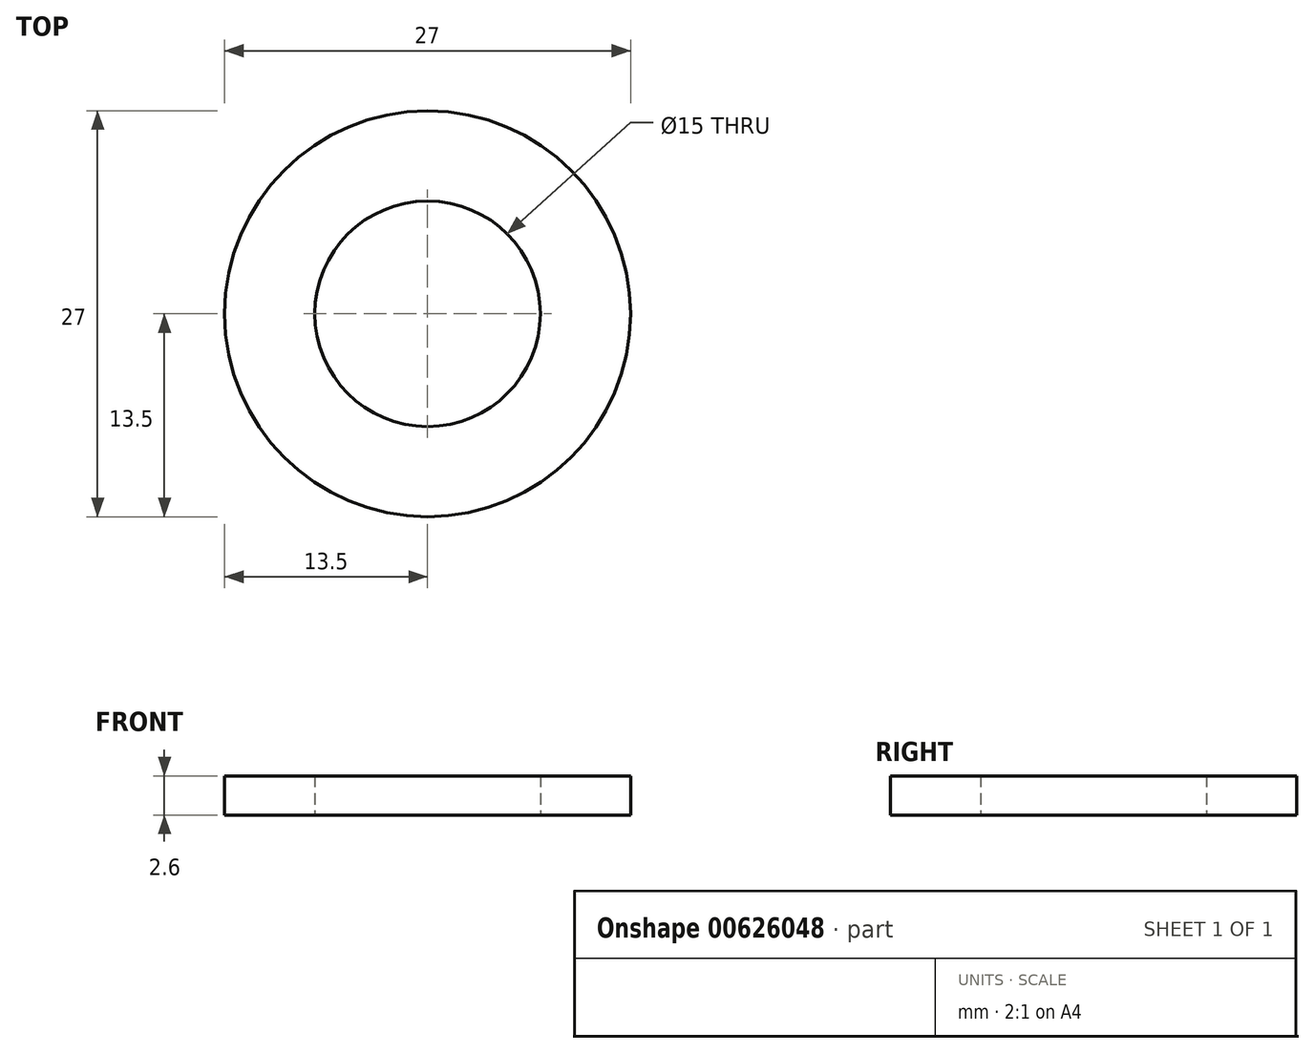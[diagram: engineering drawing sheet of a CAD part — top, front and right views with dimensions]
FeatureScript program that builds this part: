
annotation { "Feature Type Name" : "Feature", "Feature Type Description" : "" }
export const myFeature = defineFeature(function(context is Context, id is Id, definition is map)
    precondition{}
    {
        {
            var Q0;
            Q0=qCreatedBy(makeId("Top.planeOp"),FACE);
            var sketch = newSketch(context, id + "F0", { "sketchPlane" : qUnion([Q0])});
            skCircle(sketch, "E0", {"center": v(0, 0) * mm, "radius": 7.5 * mm});
            skCircle(sketch, "E1", {"center": v(0, 0) * mm, "radius": 13.5 * mm});
            skSolve(sketch);
        }
        {
            var Q0;
            Q0=makeQuery(id+"F0.imprint","IMPRINT",FACE,{"disambiguationData":[TD([[makeQuery(id+"F0.imprint","IMPRINT",EDGE,{"derivedFrom":sQuery(id+"F0.wireOp",EDGE,"E0")}),-1.0]])]});
            extrude(context, id + "F1", {"entities" : qUnion([Q0]), "depth" : 2.6 * mm, "offsetDistance" : 25 * mm});
        }
    });
